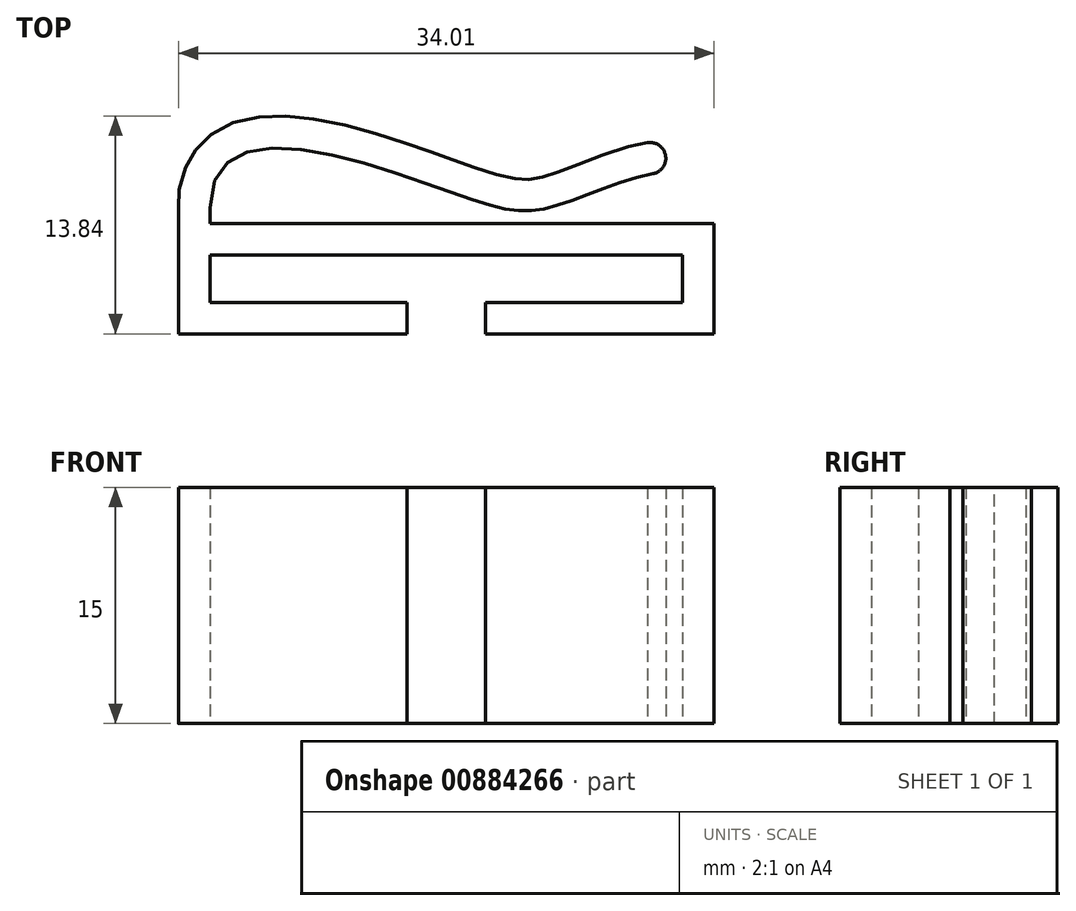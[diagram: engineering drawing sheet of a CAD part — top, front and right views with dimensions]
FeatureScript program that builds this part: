
annotation { "Feature Type Name" : "Feature", "Feature Type Description" : "" }
export const myFeature = defineFeature(function(context is Context, id is Id, definition is map)
    precondition{}
    {
        {
            var Q0;
            Q0=qCreatedBy(makeId("Top.planeOp"),FACE);
            var sketch = newSketch(context, id + "F0", { "sketchPlane" : qUnion([Q0])});
            skLineSegment(sketch, "E0", {"start": v(-14.06, 1.49) * mm, "end": v(15.94, 1.49) * mm});
            skLineSegment(sketch, "E1", {"start": v(15.94, 1.49) * mm, "end": v(15.94, -1.51) * mm});
            skLineSegment(sketch, "E2", {"start": v(15.94, -1.51) * mm, "end": v(3.44, -1.51) * mm});
            skLineSegment(sketch, "E3", {"start": v(-14.06, 1.49) * mm, "end": v(-14.06, -1.51) * mm});
            skLineSegment(sketch, "E4", {"start": v(-14.06, -1.51) * mm, "end": v(-1.56, -1.51) * mm});
            skLineSegment(sketch, "E5", {"start": v(-14.06, 3.49) * mm, "end": v(-14.06, 4.49) * mm});
            skFitSpline(sketch, "E6", {"points": [v(-14.06, 4.49) * mm, v(0.94, 5.58) * mm, v(7.37, 4.49) * mm, v(14.06, 6.66) * mm], "startDerivative": vector(0, 46.95) * mm, "endDerivative": vector(23.62, 4.24) * mm});
            skLineSegment(sketch, "E7.0", {"start": v(-16.06, -3.51) * mm, "end": v(-1.56, -3.51) * mm});
            skLineSegment(sketch, "E7.1", {"start": v(-16.06, 1.49) * mm, "end": v(-16.06, -3.51) * mm});
            skLineSegment(sketch, "E7.2", {"start": v(-16.06, 1.49) * mm, "end": v(-16.06, 4.49) * mm});
            skFitSpline(sketch, "E7.3", {"points": [v(-16.06, 4.49) * mm, v(-16.06, 5.12) * mm, v(-15.96, 6.03) * mm, v(-15.58, 7.14) * mm, v(-15.16, 7.91) * mm, v(-14.62, 8.58) * mm, v(-13.77, 9.32) * mm, v(-12.57, 9.93) * mm, v(-11.07, 10.26) * mm, v(-9.54, 10.32) * mm, v(-8, 10.2) * mm, v(-5.91, 9.85) * mm, v(-3.83, 9.3) * mm, v(-1.84, 8.68) * mm, v(-0.43, 8.2) * mm, v(0.87, 7.73) * mm, v(2, 7.33) * mm, v(2.97, 6.99) * mm, v(4.06, 6.63) * mm, v(4.88, 6.42) * mm, v(5.5, 6.32) * mm, v(5.87, 6.3) * mm, v(6.23, 6.3) * mm, v(6.6, 6.36) * mm, v(7.05, 6.46) * mm, v(7.6, 6.62) * mm, v(8.2, 6.84) * mm, v(9.1, 7.17) * mm, v(10.35, 7.66) * mm, v(11.96, 8.23) * mm, v(13.11, 8.53) * mm, v(13.7, 8.63) * mm]});
            skLineSegment(sketch, "E8.0", {"start": v(17.94, -3.51) * mm, "end": v(3.44, -3.51) * mm});
            skLineSegment(sketch, "E8.1", {"start": v(17.94, 3.49) * mm, "end": v(17.94, -3.51) * mm});
            skLineSegment(sketch, "E8.2", {"start": v(-14.06, 3.49) * mm, "end": v(17.94, 3.49) * mm});
            skArc(sketch, "E9", {"start": v(13.7, 8.63) * mm, "mid": v(14.87, 7.82) * mm, "end": v(14.06, 6.66) * mm});
            skLineSegment(sketch, "E10", {"start": v(-1.56, -1.51) * mm, "end": v(-1.56, -3.51) * mm});
            skLineSegment(sketch, "E11", {"start": v(3.44, -1.51) * mm, "end": v(3.44, -3.51) * mm});
            skSolve(sketch);
        }
        {
            var Q0;
            Q0=makeQuery(id+"F0.imprint","IMPRINT",FACE,{"disambiguationData":[TD([[makeQuery(id+"F0.imprint","IMPRINT",EDGE,{"derivedFrom":sQuery(id+"F0.wireOp",EDGE,"E0")}),1.0]])]});
            var Q1;
            Q1 = qConstructionFilter(qBodyType(qCreatedBy(id + "F0" ,EDGE), BodyType.WIRE), ConstructionObject.NO);
            extrude(context, id + "F1", {"entities" : qUnion([Q0]), "surfaceEntities" : qUnion([Q1]), "depth" : 15 * mm, "offsetDistance" : 25 * mm});
        }
    });
